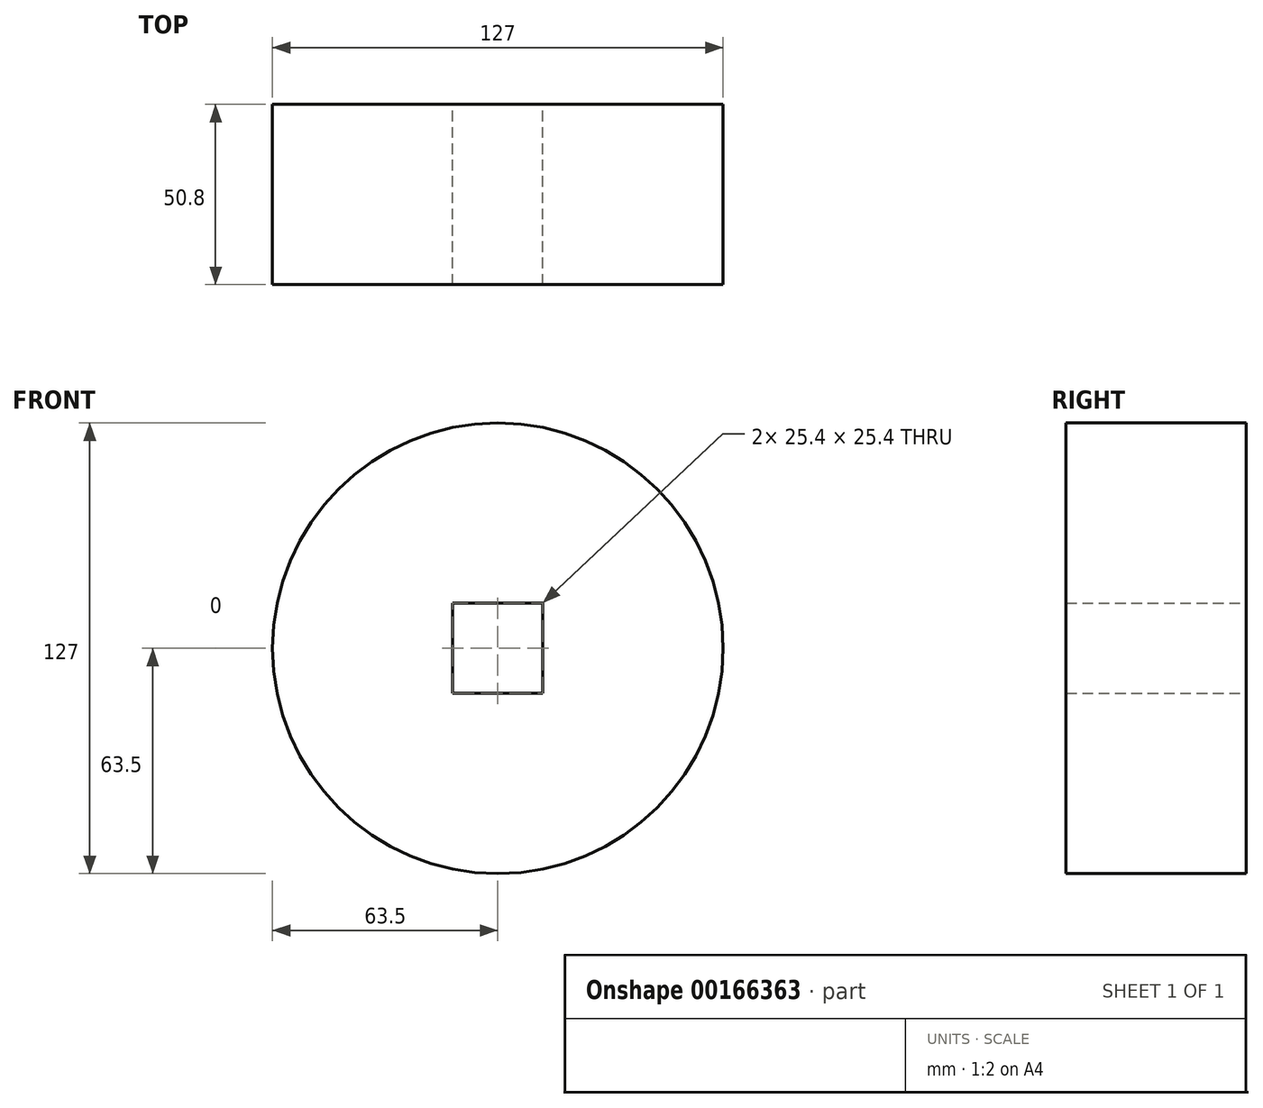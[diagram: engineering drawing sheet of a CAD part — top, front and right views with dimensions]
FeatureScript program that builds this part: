
annotation { "Feature Type Name" : "Feature", "Feature Type Description" : "" }
export const myFeature = defineFeature(function(context is Context, id is Id, definition is map)
    precondition{}
    {
        {
            var Q0;
            Q0=qCreatedBy(makeId("Front.planeOp"),FACE);
            var sketch = newSketch(context, id + "F0", { "sketchPlane" : qUnion([Q0])});
            skCircle(sketch, "E0", {"center": v(0, 0) * mm, "radius": 63.5 * mm});
            skLineSegment(sketch, "E1.bottom", {"start": v(12.7, 12.7) * mm, "end": v(-12.7, 12.7) * mm});
            skLineSegment(sketch, "E1.top", {"start": v(12.7, -12.7) * mm, "end": v(-12.7, -12.7) * mm});
            skLineSegment(sketch, "E1.left", {"start": v(12.7, 12.7) * mm, "end": v(12.7, -12.7) * mm});
            skLineSegment(sketch, "E1.right", {"start": v(-12.7, 12.7) * mm, "end": v(-12.7, -12.7) * mm});
            skSolve(sketch);
        }
        {
            var Q0;
            Q0 = qSketchRegion(id + "F0", true);
            extrude(context, id + "F1", {"entities" : qUnion([Q0]), "depth" : 50.8 * mm});
        }
    });
